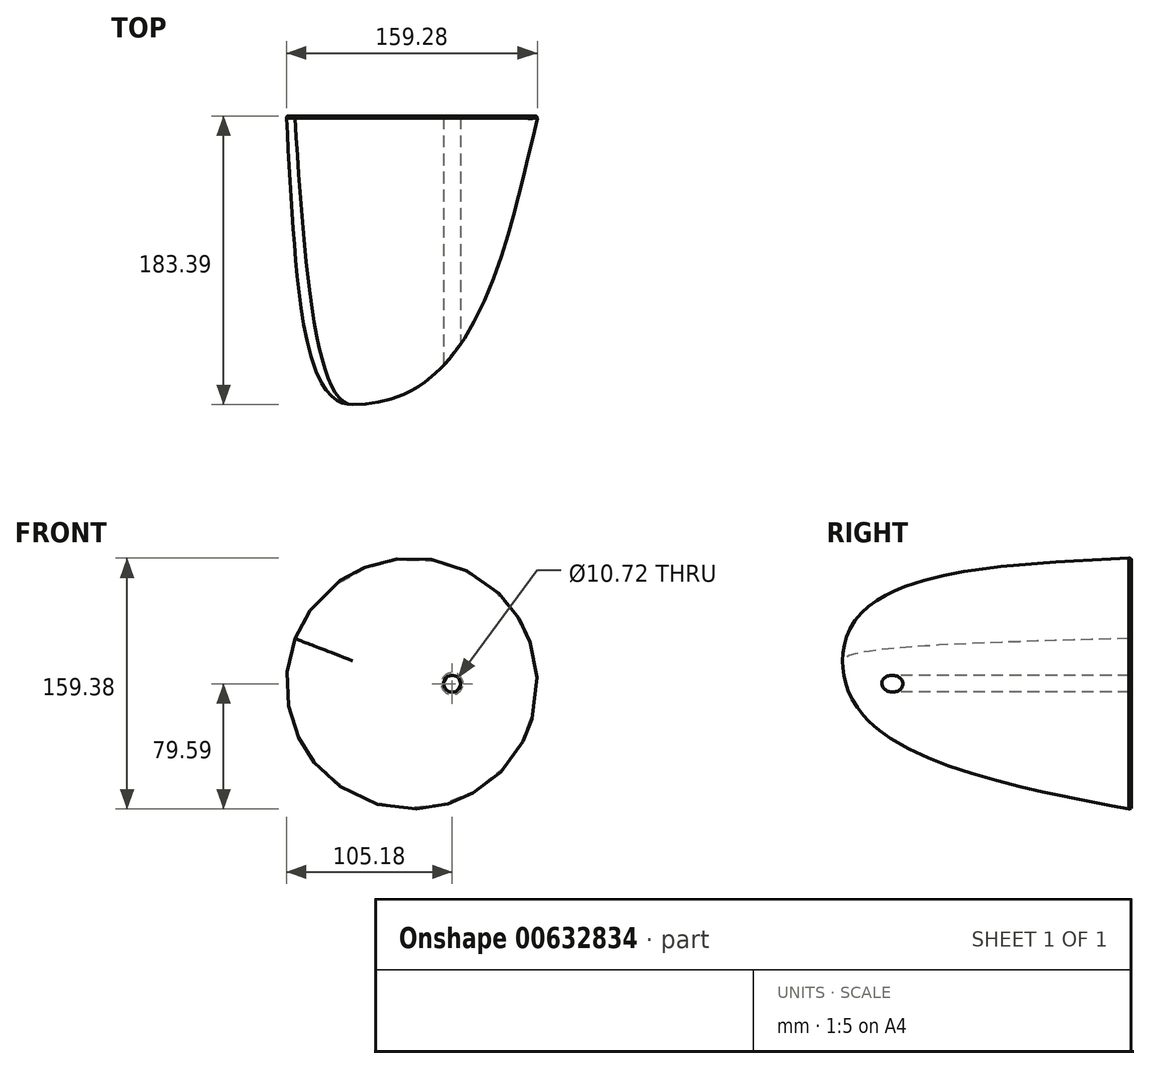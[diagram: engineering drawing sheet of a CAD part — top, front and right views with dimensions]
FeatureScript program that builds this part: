
annotation { "Feature Type Name" : "Feature", "Feature Type Description" : "" }
export const myFeature = defineFeature(function(context is Context, id is Id, definition is map)
    precondition{}
    {
        {
            var Q0;
            Q0=qCreatedBy(makeId("Front.planeOp"),FACE);
            var sketch = newSketch(context, id + "F0", { "sketchPlane" : qUnion([Q0])});
            skCircle(sketch, "E0", {"center": v(0, 0) * mm, "radius": 79.86 * mm});
            skSolve(sketch);
        }
        {
            var Q0;
            Q0=qCreatedBy(makeId("Front.planeOp"),FACE);
            cPlane(context, id + "F1", {"entities" : qUnion([Q0]), "cplaneType" : CPlaneType.OFFSET, "offset" : 183.39 * mm, "width" : 152.4 * mm, "height" : 152.4 * mm});
        }
        {
            var Q0;
            Q0=qCreatedBy(id+"F1.planeOp",FACE);
            var sketch = newSketch(context, id + "F2", { "sketchPlane" : qUnion([Q0])});
            skPoint(sketch, "E1", {"position": v(-37.7, 14.52) * mm});
            skSolve(sketch);
        }
        {
            var Q0;
            Q0=makeQuery(id+"F0.imprint","IMPRINT",FACE,{"disambiguationData":[TD([[makeQuery(id+"F0.imprint","IMPRINT",EDGE,{"derivedFrom":sQuery(id+"F0.wireOp",EDGE,"E0")}),1.0]])]});
            var Q1;
            Q1=sQuery(id+"F2.wireOp",VERTEX,"E1");
            loft(context, id + "F3", {"endCondition" : LoftEndDerivativeType.TANGENT_TO_PROFILE, "endMagnitude" : 2, "sheetProfilesArray" : [{ "sheetProfileEntities" : qUnion([Q0]) }, { "sheetProfileEntities" : qUnion([Q1]) }]});
        }
        {
            var Q0;
            Q0=makeQuery(id+"F3.opLoft","CAP_FACE",FACE,{"disambiguationData":[OSD([makeQuery(id+"F0.imprint","IMPRINT",FACE,{"disambiguationData":[TD([[makeQuery(id+"F0.imprint","IMPRINT",EDGE,{"derivedFrom":sQuery(id+"F0.wireOp",EDGE,"E0")}),1.0]])]})])],"isStart":true});
            var sketch = newSketch(context, id + "F4", { "sketchPlane" : qUnion([Q0])});
            skPoint(sketch, "E2", {"position": v(-25.4, 0) * mm});
            skSolve(sketch);
        }
        {
            var Q0;
            Q0=sQuery(id+"F4.wireOp",VERTEX,"E2");
            var Q1;
            Q1=makeQuery(id+"F3.opLoft","SWEPT_BODY",BODY,{"disambiguationData":[OSD([makeQuery(id+"F0.imprint","IMPRINT",FACE,{"disambiguationData":[TD([[makeQuery(id+"F0.imprint","IMPRINT",EDGE,{"derivedFrom":sQuery(id+"F0.wireOp",EDGE,"E0")}),1.0]])]}),sQuery(id+"F2.wireOp",VERTEX,"E1")])]});
            hole(context, id + "F5", {"style" : HoleStyle.SIMPLE, "endStyle" : HoleEndStyle.THROUGH, "standardTappedOrClearance" : lookupTablePath({ "standard" : "ANSI", "fit" : "Normal (ASME)", "engagement" : "75%", "pitch" : "13 tpi", "size" : "1/2", "type" : "Tapped" }), "standardBlindInLast" : lookupTablePath({ "fit" : "Free", "standard" : "ANSI", "engagement" : "75%", "pitch" : "13 tpi", "size" : "1/2", "type" : "Tapped" }), "holeDiameter" : 10.72 * mm, "majorDiameter" : 12.7 * mm, "showTappedDepth" : true, "tappedDepth" : 12.7 * mm, "tapClearance" : 3, "locations" : qUnion([Q0]), "scope" : qUnion([Q1]), "startStyle" : HoleStartStyle.PART});
        }
        {
            var Q0;
            Q0=makeQuery(id+"F3.opLoft","CAP_FACE",FACE,{"disambiguationData":[OSD([makeQuery(id+"F0.imprint","IMPRINT",FACE,{"disambiguationData":[TD([[makeQuery(id+"F0.imprint","IMPRINT",EDGE,{"derivedFrom":sQuery(id+"F0.wireOp",EDGE,"E0")}),1.0]])]})])],"isStart":true});
            chamfer(context, id + "F6", {"entities" : qUnion([Q0]), "chamferType" : ChamferType.OFFSET_ANGLE, "width" : 1.59 * mm, "oppositeDirection" : false, "angle" : 30 * degree, "tangentPropagation" : true});
        }
    });
